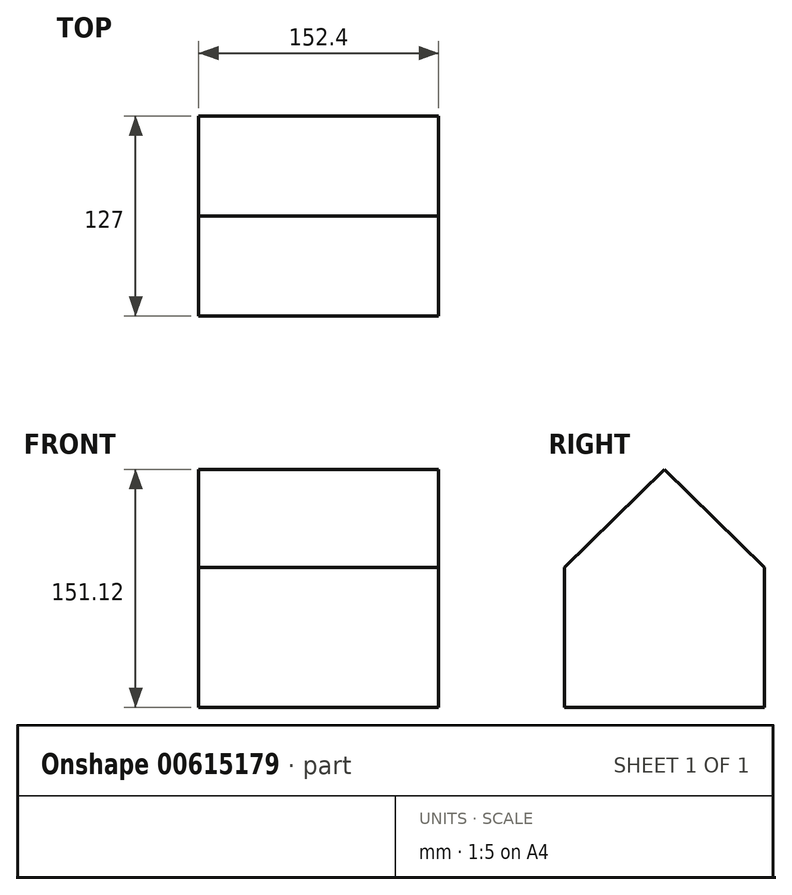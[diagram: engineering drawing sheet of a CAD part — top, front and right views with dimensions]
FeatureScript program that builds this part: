
annotation { "Feature Type Name" : "Feature", "Feature Type Description" : "" }
export const myFeature = defineFeature(function(context is Context, id is Id, definition is map)
    precondition{}
    {
        {
            var Q0;
            Q0=qCreatedBy(makeId("Front.planeOp"),FACE);
            var sketch = newSketch(context, id + "F0", { "sketchPlane" : qUnion([Q0])});
            skLineSegment(sketch, "E0.bottom", {"start": v(76.2, 44.45) * mm, "end": v(-76.2, 44.45) * mm});
            skLineSegment(sketch, "E0.top", {"start": v(76.2, -44.45) * mm, "end": v(-76.2, -44.45) * mm});
            skLineSegment(sketch, "E0.left", {"start": v(76.2, 44.45) * mm, "end": v(76.2, -44.45) * mm});
            skLineSegment(sketch, "E0.right", {"start": v(-76.2, 44.45) * mm, "end": v(-76.2, -44.45) * mm});
            skPoint(sketch, "E0.middle", {"position": v(0, 0) * mm});
            skSolve(sketch);
        }
        {
            var Q0;
            Q0 = qSketchRegion(id + "F0", true);
            extrude(context, id + "F1", {"entities" : qUnion([Q0]), "depth" : 127 * mm, "offsetDistance" : 25.4 * mm});
        }
        {
            var Q0;
            Q0=makeQuery(id+"F1.opExtrude","SWEPT_FACE",FACE,{"disambiguationData":[OSD([sQuery(id+"F0.wireOp",EDGE,"E0.left")])]});
            var sketch = newSketch(context, id + "F2", { "sketchPlane" : qUnion([Q0])});
            skLineSegment(sketch, "E1", {"start": v(-127, 44.45) * mm, "end": v(-63.5, 106.67) * mm});
            skLineSegment(sketch, "E2", {"start": v(-63.5, 106.67) * mm, "end": v(0, 44.45) * mm});
            skSolve(sketch);
        }
        {
            var Q0;
            Q0=makeQuery(id+"F2.imprint","IMPRINT",FACE,{"disambiguationData":[TD([[makeQuery(id+"F2.imprint","IMPRINT",EDGE,{"derivedFrom":sQuery(id+"F2.wireOp",EDGE,"E1")}),-1.0]])]});
            extrude(context, id + "F3", {"entities" : qUnion([Q0]), "operationType" : NewBodyOperationType.ADD, "depth" : -152.4 * mm, "offsetDistance" : 25.4 * mm});
        }
    });
